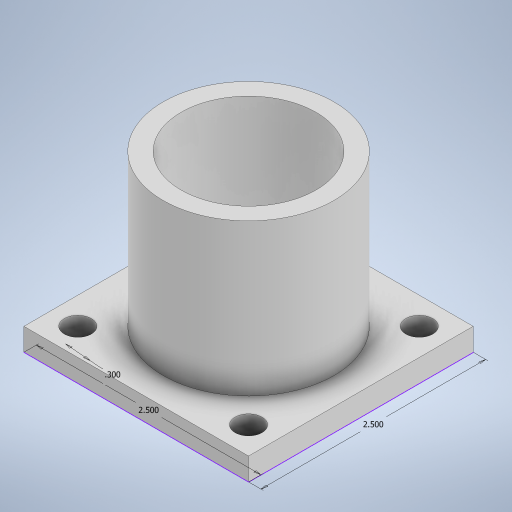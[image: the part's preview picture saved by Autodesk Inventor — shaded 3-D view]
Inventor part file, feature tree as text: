
AUTODESK INVENTOR PART (.ipt)
format: ipt  version: 2023 (Build 270158000, 158)  size: 268,800 bytes
history: native  units: in
note: dims shown in document units (in); Inventor stores cm internally (conversion verified against a paired STEP export)
features: extrude x3, sketch x1
ambient origin geometry x8: Origin, YZ Plane, XZ Plane, XY Plane, X Axis, Y Axis, Z Axis, Center Point
bodies: Solid1 (feature_tree)
feature tree (4):
  sketch  "Sketch1"  dims[d6=1.938in d7=0.0in d10=2.5in d11=2.5in d12=0.25in d13=0.0in d14=0.3in d15=0.25in d16=0.0in]
  extrude  "Extrusion1"  Depth=2.5in
  extrude  "Extrusion3"  Depth=2.5in
  extrude  "Extrusion4"  Depth=0.25in TaperAngle=0.0deg
